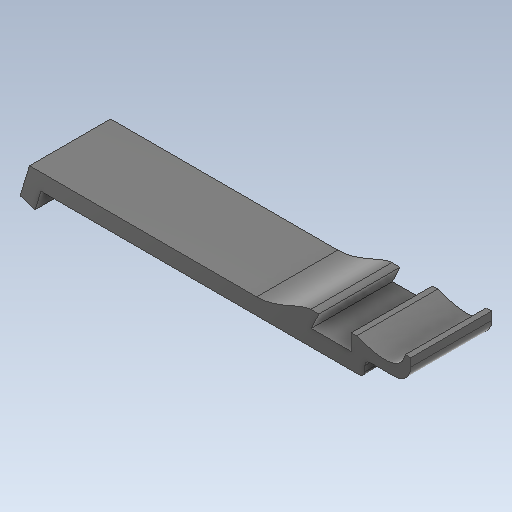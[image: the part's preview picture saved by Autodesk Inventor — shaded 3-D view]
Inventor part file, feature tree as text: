
AUTODESK INVENTOR PART (.ipt)
format: ipt  version: 2020 (Build 240168000, 168)  size: 224,256 bytes
history: native  units: mm
features: extrude x4, sketch x3, projected_geometry x2, other x1
ambient origin geometry x8: Origin, YZ Plane, XZ Plane, XY Plane, X Axis, Y Axis, Z Axis, Center Point
bodies: Body1 (feature_tree)
feature tree (10):
  other  "Твердое тело1"
  extrude  "Выдавливание1"  Depth=9.0mm
  extrude  "Выдавливание2"  Depth=3.0mm
  sketch  "Эскиз4"
  extrude  "Выдавливание3"  Depth=3.0mm
  extrude  "Выдавливание4"  Depth=2.5mm
  sketch  "Эскиз1"
  sketch  "Эскиз3"
  projected_geometry  "Спроецированная петля1"
  projected_geometry  "Спроецированная петля2"
